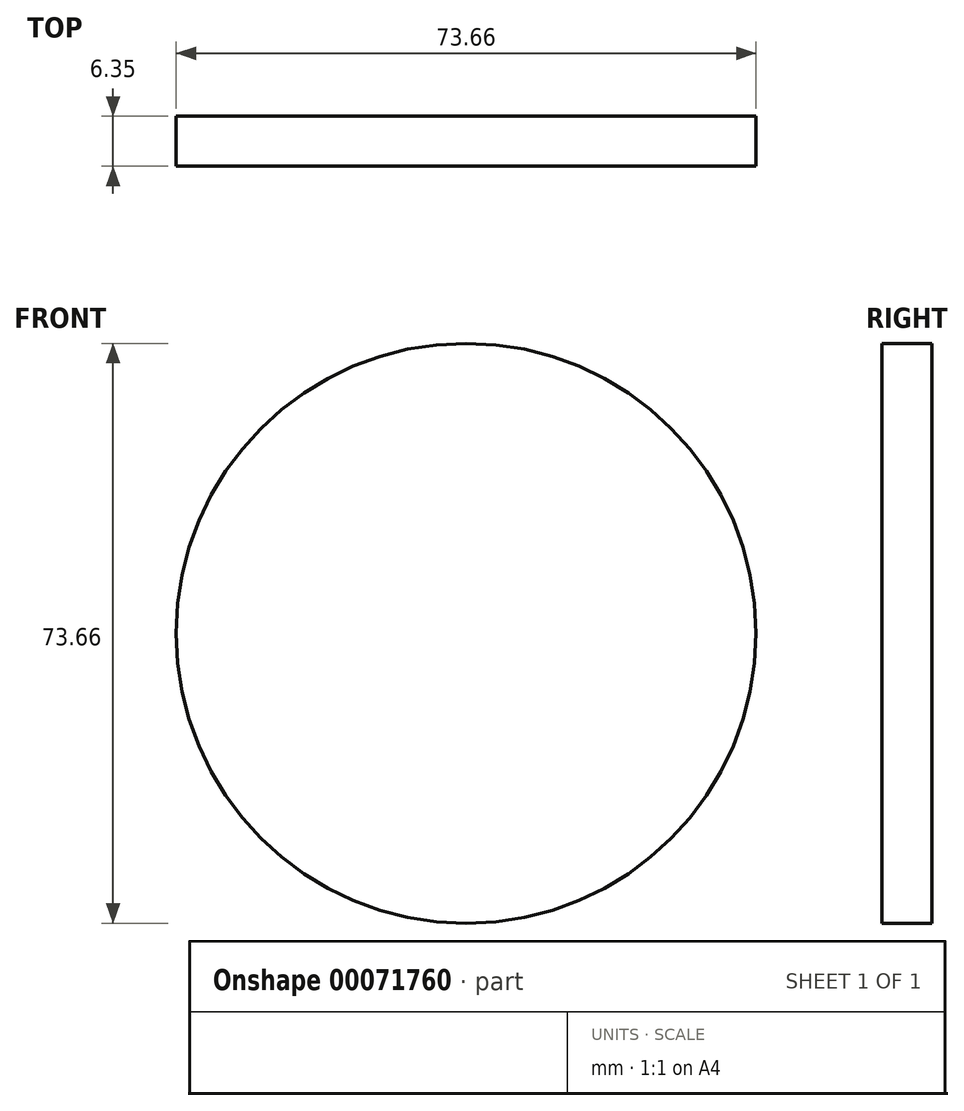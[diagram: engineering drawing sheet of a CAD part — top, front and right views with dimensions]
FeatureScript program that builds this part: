
annotation { "Feature Type Name" : "Feature", "Feature Type Description" : "" }
export const myFeature = defineFeature(function(context is Context, id is Id, definition is map)
    precondition{}
    {
        {
            var Q0;
            Q0=qCreatedBy(makeId("Front.planeOp"),FACE);
            var sketch = newSketch(context, id + "F0", { "sketchPlane" : qUnion([Q0])});
            skCircle(sketch, "E0", {"center": v(0, 0) * mm, "radius": 36.83 * mm});
            skSolve(sketch);
        }
        {
            var Q0;
            Q0=makeQuery(id+"F0.imprint","IMPRINT",FACE,{"disambiguationData":[TD([[makeQuery(id+"F0.imprint","IMPRINT",EDGE,{"derivedFrom":sQuery(id+"F0.wireOp",EDGE,"E0")}),1.0]])]});
            extrude(context, id + "F1", {"entities" : qUnion([Q0]), "depth" : 6.35 * mm});
        }
    });
